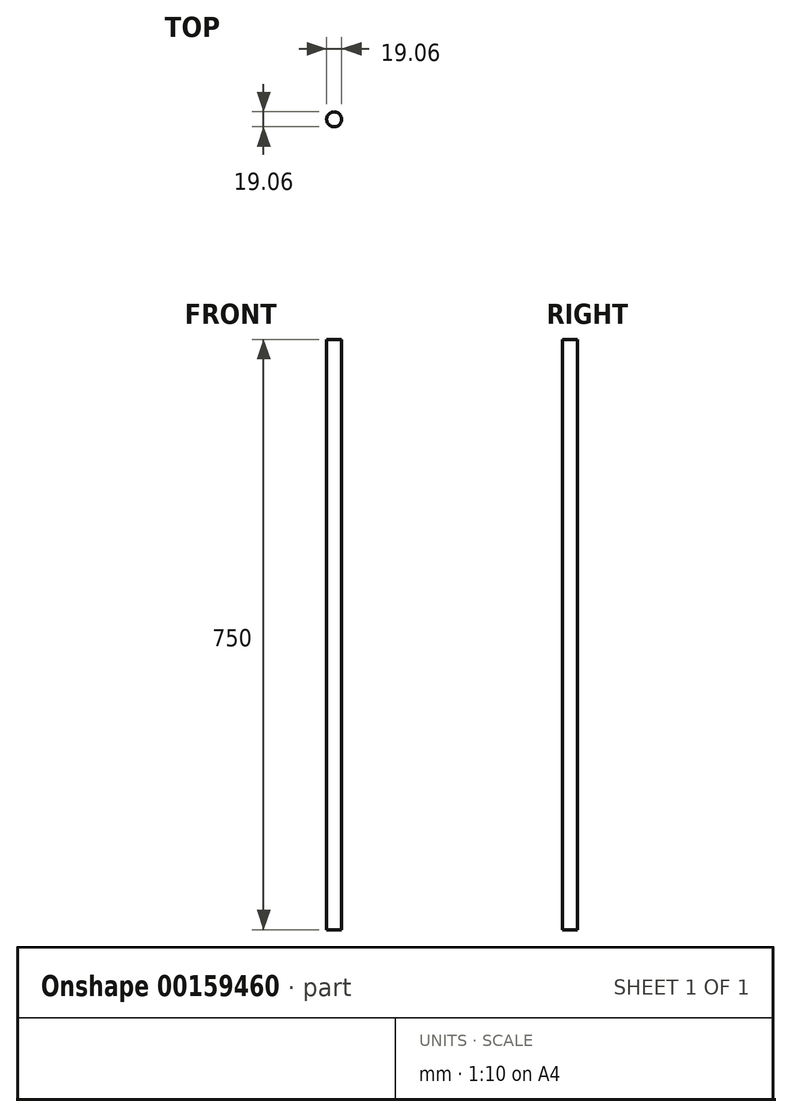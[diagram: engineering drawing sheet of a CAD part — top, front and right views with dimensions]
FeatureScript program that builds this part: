
annotation { "Feature Type Name" : "Feature", "Feature Type Description" : "" }
export const myFeature = defineFeature(function(context is Context, id is Id, definition is map)
    precondition{}
    {
        {
            var Q0;
            Q0=qCreatedBy(makeId("Top.planeOp"),FACE);
            var sketch = newSketch(context, id + "F0", { "sketchPlane" : qUnion([Q0])});
            skCircle(sketch, "E0", {"center": v(0, 0) * mm, "radius": 9.53 * mm});
            skSolve(sketch);
        }
        {
            var Q0;
            Q0 = qSketchRegion(id + "F0", true);
            var Q1;
            Q1=sQuery(id+"F0.wireOp",EDGE,"E0");
            extrude(context, id + "F1", {"entities" : qUnion([Q0]), "surfaceEntities" : qUnion([Q1]), "depth" : 750 * mm});
        }
    });
